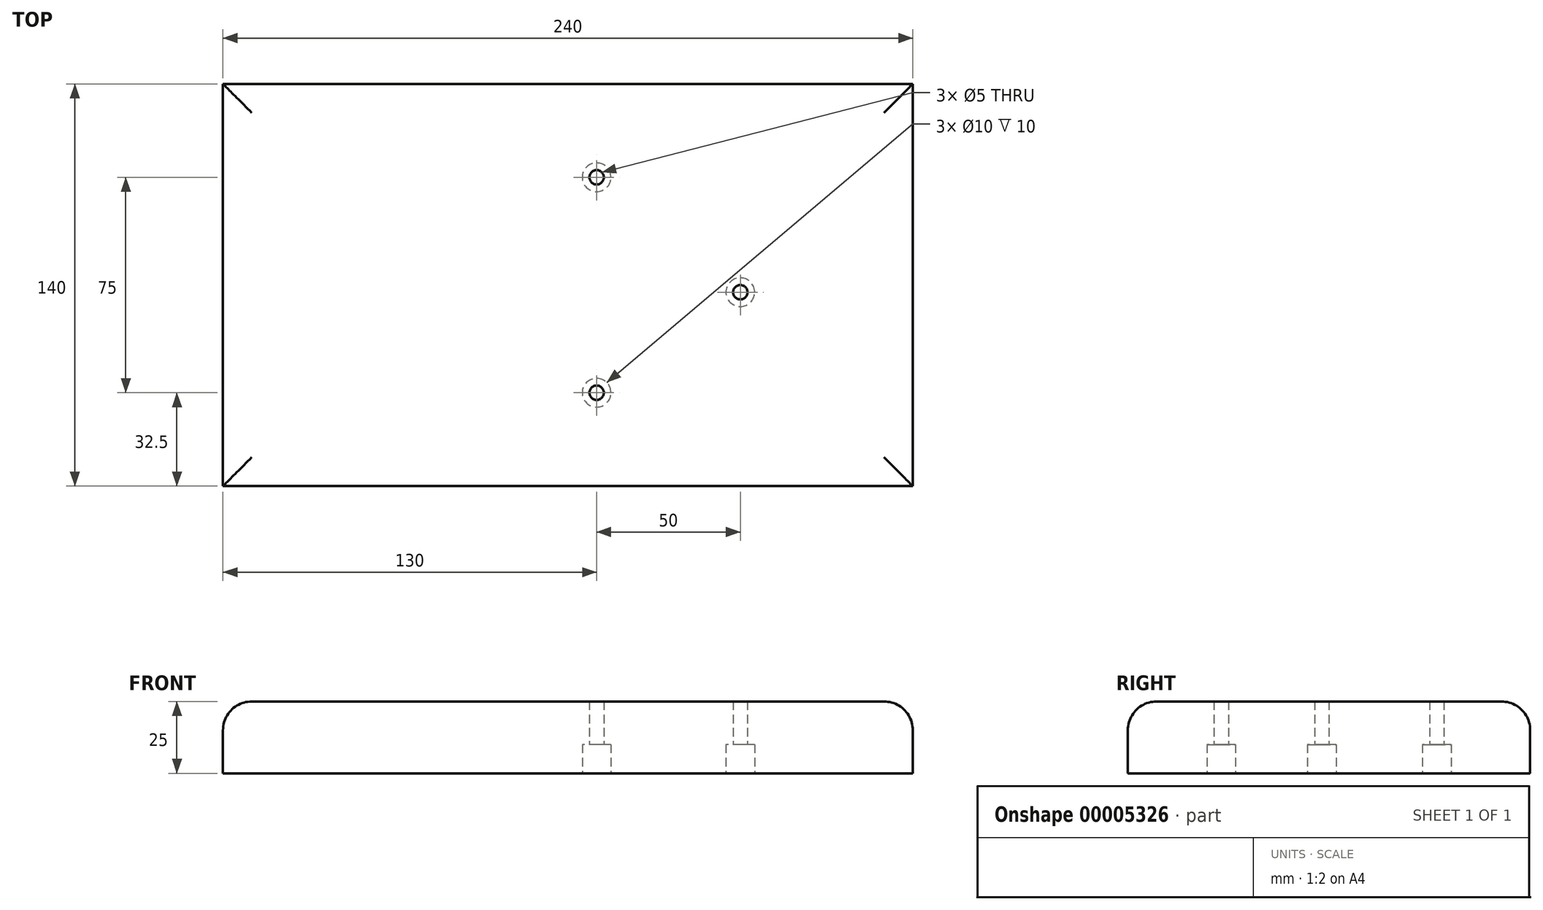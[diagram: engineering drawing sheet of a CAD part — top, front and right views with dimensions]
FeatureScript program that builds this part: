
annotation { "Feature Type Name" : "Feature", "Feature Type Description" : "" }
export const myFeature = defineFeature(function(context is Context, id is Id, definition is map)
    precondition{}
    {
        {
            var Q0;
            Q0=qCreatedBy(makeId("Top.planeOp"),FACE);
            var sketch = newSketch(context, id + "F0", { "sketchPlane" : qUnion([Q0])});
            skLineSegment(sketch, "E0.bottom", {"start": v(0, 0) * mm, "end": v(240, 0) * mm});
            skLineSegment(sketch, "E0.top", {"start": v(0, 140) * mm, "end": v(240, 140) * mm});
            skLineSegment(sketch, "E0.left", {"start": v(0, 0) * mm, "end": v(0, 140) * mm});
            skLineSegment(sketch, "E0.right", {"start": v(240, 0) * mm, "end": v(240, 140) * mm});
            skCircle(sketch, "E1", {"center": v(130, 107.5) * mm, "radius": 2.5 * mm});
            skCircle(sketch, "E2", {"center": v(180, 67.5) * mm, "radius": 2.5 * mm});
            skCircle(sketch, "E3", {"center": v(130, 32.5) * mm, "radius": 2.5 * mm});
            skCircle(sketch, "E4", {"center": v(130, 107.5) * mm, "radius": 5 * mm});
            skCircle(sketch, "E5", {"center": v(180, 67.5) * mm, "radius": 5 * mm});
            skCircle(sketch, "E6", {"center": v(130, 32.5) * mm, "radius": 5 * mm});
            skSolve(sketch);
        }
        {
            var Q0;
            Q0=makeQuery(id+"F0.imprint","IMPRINT",FACE,{"disambiguationData":[TD([[makeQuery(id+"F0.imprint","IMPRINT",EDGE,{"derivedFrom":sQuery(id+"F0.wireOp",EDGE,"E0.bottom")}),1.0]])]});
            var Q1;
            Q1=makeQuery(id+"F0.imprint","IMPRINT",FACE,{"disambiguationData":[TD([[makeQuery(id+"F0.imprint","IMPRINT",EDGE,{"derivedFrom":sQuery(id+"F0.wireOp",EDGE,"E1")}),-1.0]])]});
            var Q2;
            Q2=makeQuery(id+"F0.imprint","IMPRINT",FACE,{"disambiguationData":[TD([[makeQuery(id+"F0.imprint","IMPRINT",EDGE,{"derivedFrom":sQuery(id+"F0.wireOp",EDGE,"E2")}),-1.0]])]});
            var Q3;
            Q3=makeQuery(id+"F0.imprint","IMPRINT",FACE,{"disambiguationData":[TD([[makeQuery(id+"F0.imprint","IMPRINT",EDGE,{"derivedFrom":sQuery(id+"F0.wireOp",EDGE,"E3")}),-1.0]])]});
            extrude(context, id + "F1", {"entities" : qUnion([Q0, Q1, Q2, Q3]), "depth" : 25 * mm});
        }
        {
            var Q0;
            Q0=makeQuery(id+"F0.imprint","IMPRINT",FACE,{"disambiguationData":[TD([[makeQuery(id+"F0.imprint","IMPRINT",EDGE,{"derivedFrom":sQuery(id+"F0.wireOp",EDGE,"E3")}),-1.0]])]});
            var Q1;
            Q1=makeQuery(id+"F0.imprint","IMPRINT",FACE,{"disambiguationData":[TD([[makeQuery(id+"F0.imprint","IMPRINT",EDGE,{"derivedFrom":sQuery(id+"F0.wireOp",EDGE,"E2")}),-1.0]])]});
            var Q2;
            Q2=makeQuery(id+"F0.imprint","IMPRINT",FACE,{"disambiguationData":[TD([[makeQuery(id+"F0.imprint","IMPRINT",EDGE,{"derivedFrom":sQuery(id+"F0.wireOp",EDGE,"E1")}),-1.0]])]});
            extrude(context, id + "F2", {"entities" : qUnion([Q0, Q1, Q2]), "operationType" : NewBodyOperationType.REMOVE, "depth" : 10 * mm});
        }
        {
            var Q0;
            Q0=makeQuery(id+"F1.opExtrude","CAP_EDGE",EDGE,{"disambiguationData":[OSD([sQuery(id+"F0.wireOp",EDGE,"E0.bottom")])],"isStart":false});
            var Q1;
            Q1=makeQuery(id+"F1.opExtrude","CAP_EDGE",EDGE,{"disambiguationData":[OSD([sQuery(id+"F0.wireOp",EDGE,"E0.right")])],"isStart":false});
            var Q2;
            Q2=makeQuery(id+"F1.opExtrude","CAP_EDGE",EDGE,{"disambiguationData":[OSD([sQuery(id+"F0.wireOp",EDGE,"E0.top")])],"isStart":false});
            var Q3;
            Q3=makeQuery(id+"F1.opExtrude","CAP_EDGE",EDGE,{"disambiguationData":[OSD([sQuery(id+"F0.wireOp",EDGE,"E0.left")])],"isStart":false});
            fillet(context, id + "F3", {"entities" : qUnion([Q0, Q1, Q2, Q3]), "radius" : 10 * mm, "tangentPropagation" : true, "allowEdgeOverflow" : false});
        }
    });
